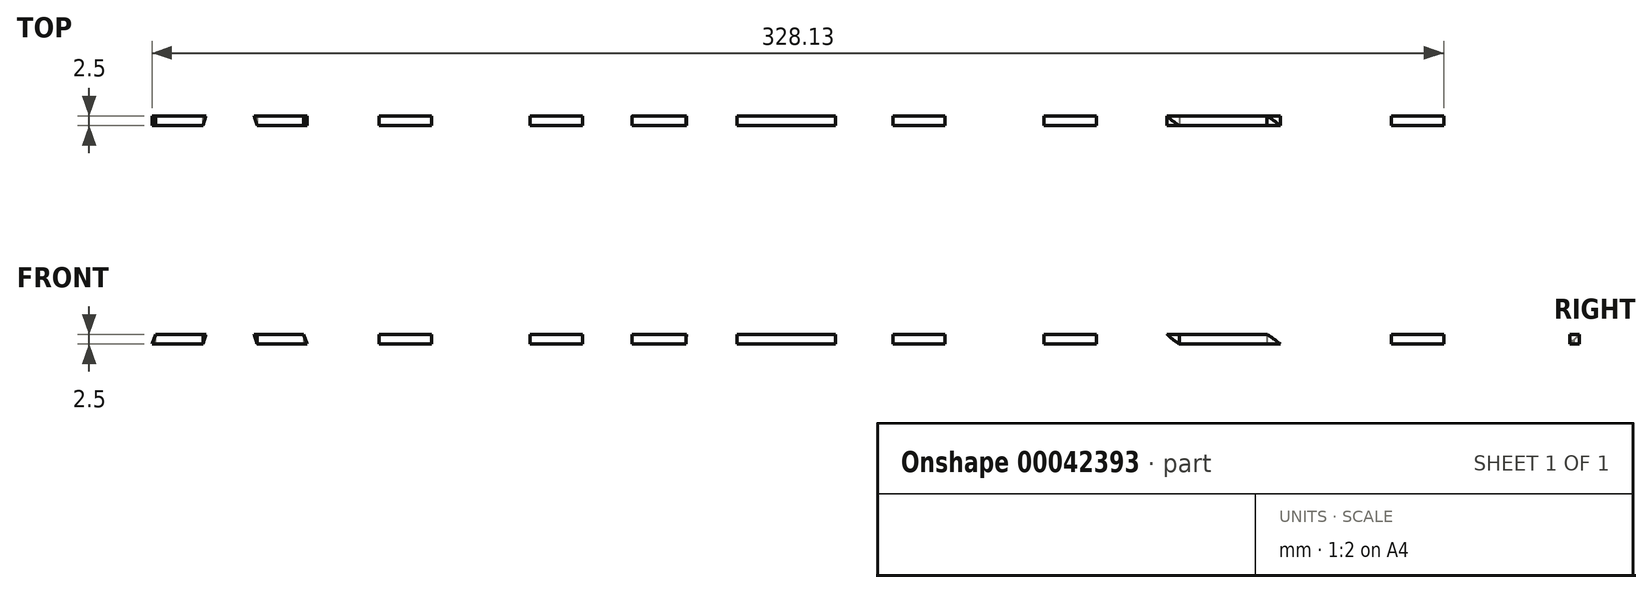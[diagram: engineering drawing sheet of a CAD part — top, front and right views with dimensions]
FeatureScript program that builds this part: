
annotation { "Feature Type Name" : "Feature", "Feature Type Description" : "" }
export const myFeature = defineFeature(function(context is Context, id is Id, definition is map)
    precondition{}
    {
        {
            assignVariable(context, id + "F0", {"name" : "x", "anyValue" : 2.5});
        }
        {
            var Q0;
            Q0=qCreatedBy(makeId("Top.planeOp"),FACE);
            var sketch = newSketch(context, id + "F1", { "sketchPlane" : qUnion([Q0])});
            skLineSegment(sketch, "E0.rect.bottom", {"start": v(190.5, -63.5) * mm, "end": v(-190.5, -63.5) * mm});
            skLineSegment(sketch, "E0.rect.top", {"start": v(190.5, 63.5) * mm, "end": v(-190.5, 63.5) * mm});
            skLineSegment(sketch, "E0.rect.left", {"start": v(190.5, -63.5) * mm, "end": v(190.5, 63.5) * mm});
            skLineSegment(sketch, "E0.rect.right", {"start": v(-190.5, -63.5) * mm, "end": v(-190.5, 63.5) * mm});
            skPoint(sketch, "E0.rect.middle", {"position": v(0, 0) * mm});
            skText(sketch, "E1", { "text": "AUGUST", "fontName": "OpenSans-Bold.ttf"});
            const initialGuessF1  = {"E1": [-0.17797, -0.03175, 1, 0, 0.0635]};
            skSetInitialGuess(sketch, initialGuessF1);
            skSolve(sketch);
        }
        {
            var Q0;
            Q0=makeQuery(id+"F1.imprint","IMPRINT",FACE,{"disambiguationData":[TD([[makeQuery(id+"F1.imprint","IMPRINT",EDGE,{"derivedFrom":sQuery(id+"F1.wireOp",EDGE,"E0.rect.bottom")}),-1.0]])]});
            extrude(context, id + "F2", {"entities" : qUnion([Q0]), "depth" : (getVariable(context, 'x')) * mm, "symmetric" : true});
        }
        {
            var Q0;
            Q0=makeQuery(id+"F1.imprint","IMPRINT",FACE,{"disambiguationData":[TD([[makeQuery(id+"F1.imprint","IMPRINT",EDGE,{"derivedFrom":sQuery(id+"F1.wireOp",EDGE,"E1.sketch_text.stroke-0")}),-1.0]])]});
            var Q1;
            Q1=makeQuery(id+"F1.imprint","IMPRINT",FACE,{"disambiguationData":[TD([[makeQuery(id+"F1.imprint","IMPRINT",EDGE,{"derivedFrom":sQuery(id+"F1.wireOp",EDGE,"E1.sketch_text.stroke-12")}),-1.0]])]});
            var Q2;
            Q2=makeQuery(id+"F1.imprint","IMPRINT",FACE,{"disambiguationData":[TD([[makeQuery(id+"F1.imprint","IMPRINT",EDGE,{"derivedFrom":sQuery(id+"F1.wireOp",EDGE,"E1.sketch_text.stroke-27")}),-1.0]])]});
            var Q3;
            Q3=makeQuery(id+"F1.imprint","IMPRINT",FACE,{"disambiguationData":[TD([[makeQuery(id+"F1.imprint","IMPRINT",EDGE,{"derivedFrom":sQuery(id+"F1.wireOp",EDGE,"E1.sketch_text.stroke-46")}),-1.0]])]});
            var Q4;
            Q4=makeQuery(id+"F1.imprint","IMPRINT",FACE,{"disambiguationData":[TD([[makeQuery(id+"F1.imprint","IMPRINT",EDGE,{"derivedFrom":sQuery(id+"F1.wireOp",EDGE,"E1.sketch_text.stroke-61")}),-1.0]])]});
            var Q5;
            Q5=makeQuery(id+"F1.imprint","IMPRINT",FACE,{"disambiguationData":[TD([[makeQuery(id+"F1.imprint","IMPRINT",EDGE,{"derivedFrom":sQuery(id+"F1.wireOp",EDGE,"E1.sketch_text.stroke-89")}),-1.0]])]});
            extrude(context, id + "F3", {"entities" : qUnion([Q0, Q1, Q2, Q3, Q4, Q5]), "depth" : (getVariable(context, 'x')) * mm, "symmetric" : true});
        }
        {
            var Q0;
            Q0=qCreatedBy(makeId("Front.planeOp"),FACE);
            var sketch = newSketch(context, id + "F4", { "sketchPlane" : qUnion([Q0])});
            skText(sketch, "E2", { "text": "AUGUST", "fontName": "OpenSans-Bold.ttf"});
            const initialGuessF4  = {"E2": [-0.17797, -0.03175, 1, 0, 0.0635]};
            skSetInitialGuess(sketch, initialGuessF4);
            skSolve(sketch);
        }
        {
            var Q0;
            Q0=makeQuery(id+"F4.imprint","IMPRINT",FACE,{"disambiguationData":[TD([[makeQuery(id+"F4.imprint","IMPRINT",EDGE,{"derivedFrom":sQuery(id+"F4.wireOp",EDGE,"E2.sketch_text.stroke-0")}),-1.0]])]});
            var Q1;
            Q1=makeQuery(id+"F4.imprint","IMPRINT",FACE,{"disambiguationData":[TD([[makeQuery(id+"F4.imprint","IMPRINT",EDGE,{"derivedFrom":sQuery(id+"F4.wireOp",EDGE,"E2.sketch_text.stroke-27")}),-1.0]])]});
            var Q2;
            Q2=makeQuery(id+"F4.imprint","IMPRINT",FACE,{"disambiguationData":[TD([[makeQuery(id+"F4.imprint","IMPRINT",EDGE,{"derivedFrom":sQuery(id+"F4.wireOp",EDGE,"E2.sketch_text.stroke-61")}),-1.0]])]});
            var Q3;
            Q3=makeQuery(id+"F4.imprint","IMPRINT",FACE,{"disambiguationData":[TD([[makeQuery(id+"F4.imprint","IMPRINT",EDGE,{"derivedFrom":sQuery(id+"F4.wireOp",EDGE,"E2.sketch_text.stroke-89")}),-1.0]])]});
            var Q4;
            Q4=makeQuery(id+"F4.imprint","IMPRINT",FACE,{"disambiguationData":[TD([[makeQuery(id+"F4.imprint","IMPRINT",EDGE,{"derivedFrom":sQuery(id+"F4.wireOp",EDGE,"E2.sketch_text.stroke-46")}),-1.0]])]});
            var Q5;
            Q5=makeQuery(id+"F4.imprint","IMPRINT",FACE,{"disambiguationData":[TD([[makeQuery(id+"F4.imprint","IMPRINT",EDGE,{"derivedFrom":sQuery(id+"F4.wireOp",EDGE,"E2.sketch_text.stroke-12")}),-1.0]])]});
            extrude(context, id + "F5", {"entities" : qUnion([Q0, Q1, Q2, Q3, Q4, Q5]), "operationType" : NewBodyOperationType.INTERSECT, "oppositeDirection" : true, "depth" : (getVariable(context, 'x')) * mm, "symmetric" : true});
        }
    });
